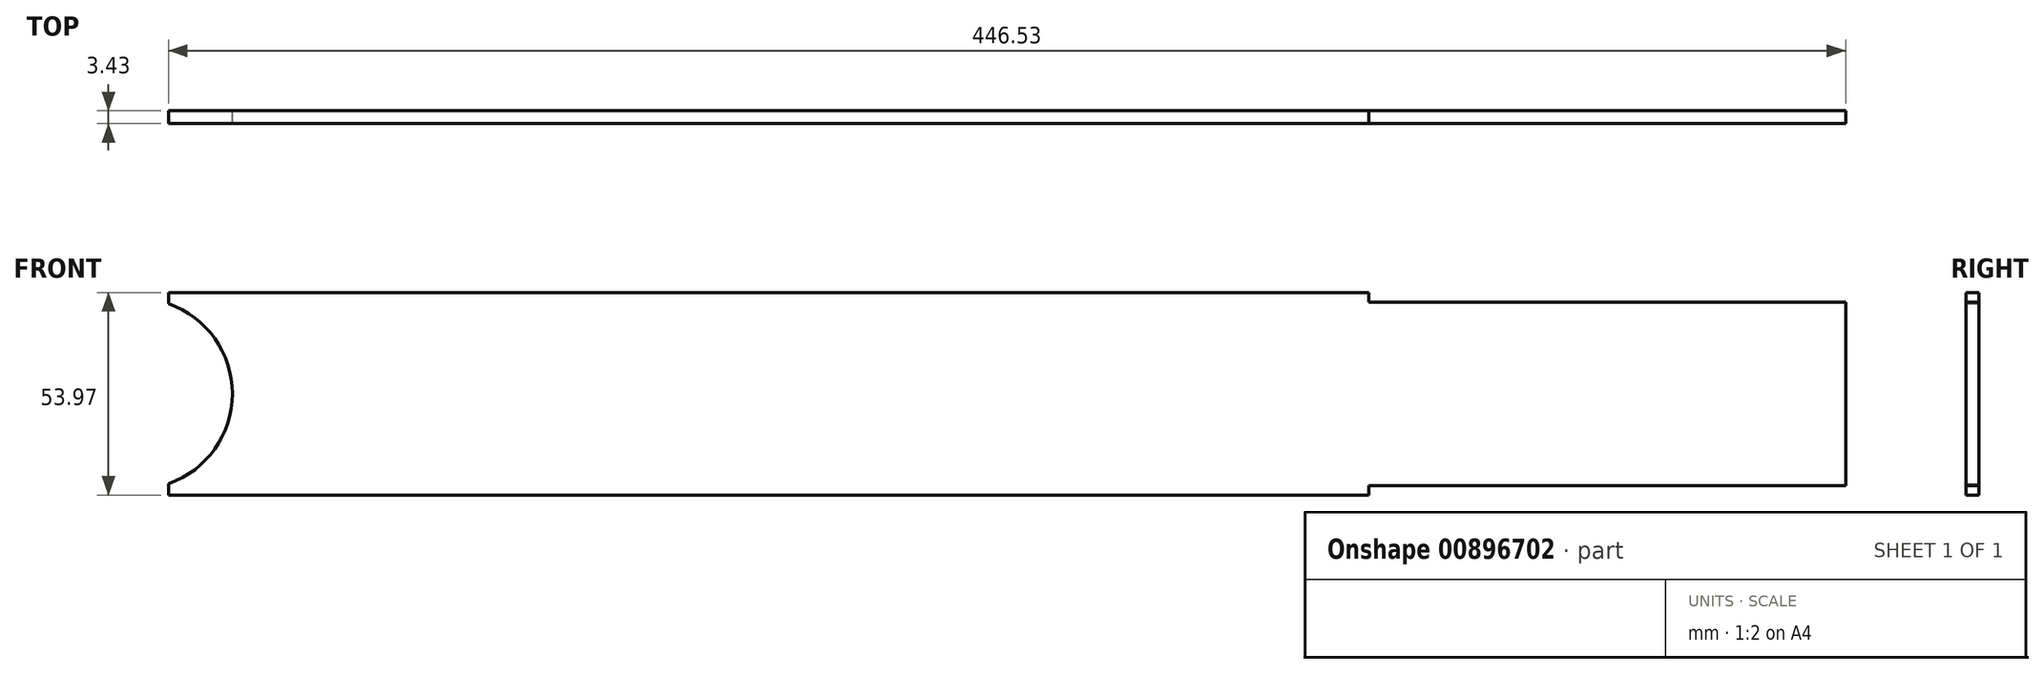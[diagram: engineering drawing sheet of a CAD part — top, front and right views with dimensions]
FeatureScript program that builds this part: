
annotation { "Feature Type Name" : "Feature", "Feature Type Description" : "" }
export const myFeature = defineFeature(function(context is Context, id is Id, definition is map)
    precondition{}
    {
        {
            var Q0;
            Q0=qCreatedBy(makeId("Front.planeOp"),FACE);
            var sketch = newSketch(context, id + "F0", { "sketchPlane" : qUnion([Q0])});
            skLineSegment(sketch, "E0", {"start": v(758.65, 428.93) * mm, "end": v(439.12, 428.93) * mm});
            skLineSegment(sketch, "E1", {"start": v(758.65, 426.4) * mm, "end": v(758.65, 428.93) * mm});
            skLineSegment(sketch, "E2", {"start": v(885.65, 426.4) * mm, "end": v(758.65, 426.4) * mm});
            skLineSegment(sketch, "E3", {"start": v(885.65, 377.5) * mm, "end": v(885.65, 426.4) * mm});
            skLineSegment(sketch, "E4", {"start": v(758.65, 377.5) * mm, "end": v(885.65, 377.5) * mm});
            skLineSegment(sketch, "E5", {"start": v(758.65, 374.96) * mm, "end": v(758.65, 377.5) * mm});
            skLineSegment(sketch, "E6", {"start": v(439.12, 374.96) * mm, "end": v(758.65, 374.96) * mm});
            skLineSegment(sketch, "E7", {"start": v(439.12, 377.97) * mm, "end": v(439.12, 374.96) * mm});
            skArc(sketch, "E8", {"start": v(439.12, 377.97) * mm, "mid": v(456.14, 401.94) * mm, "end": v(439.12, 425.92) * mm});
            skLineSegment(sketch, "E9", {"start": v(439.12, 428.93) * mm, "end": v(439.12, 425.92) * mm});
            skSolve(sketch);
        }
        {
            var Q0;
            Q0 = qSketchRegion(id + "F0", true);
            extrude(context, id + "F1", {"entities" : qUnion([Q0]), "depth" : 3.43 * mm, "offsetDistance" : 25.4 * mm});
        }
    });
